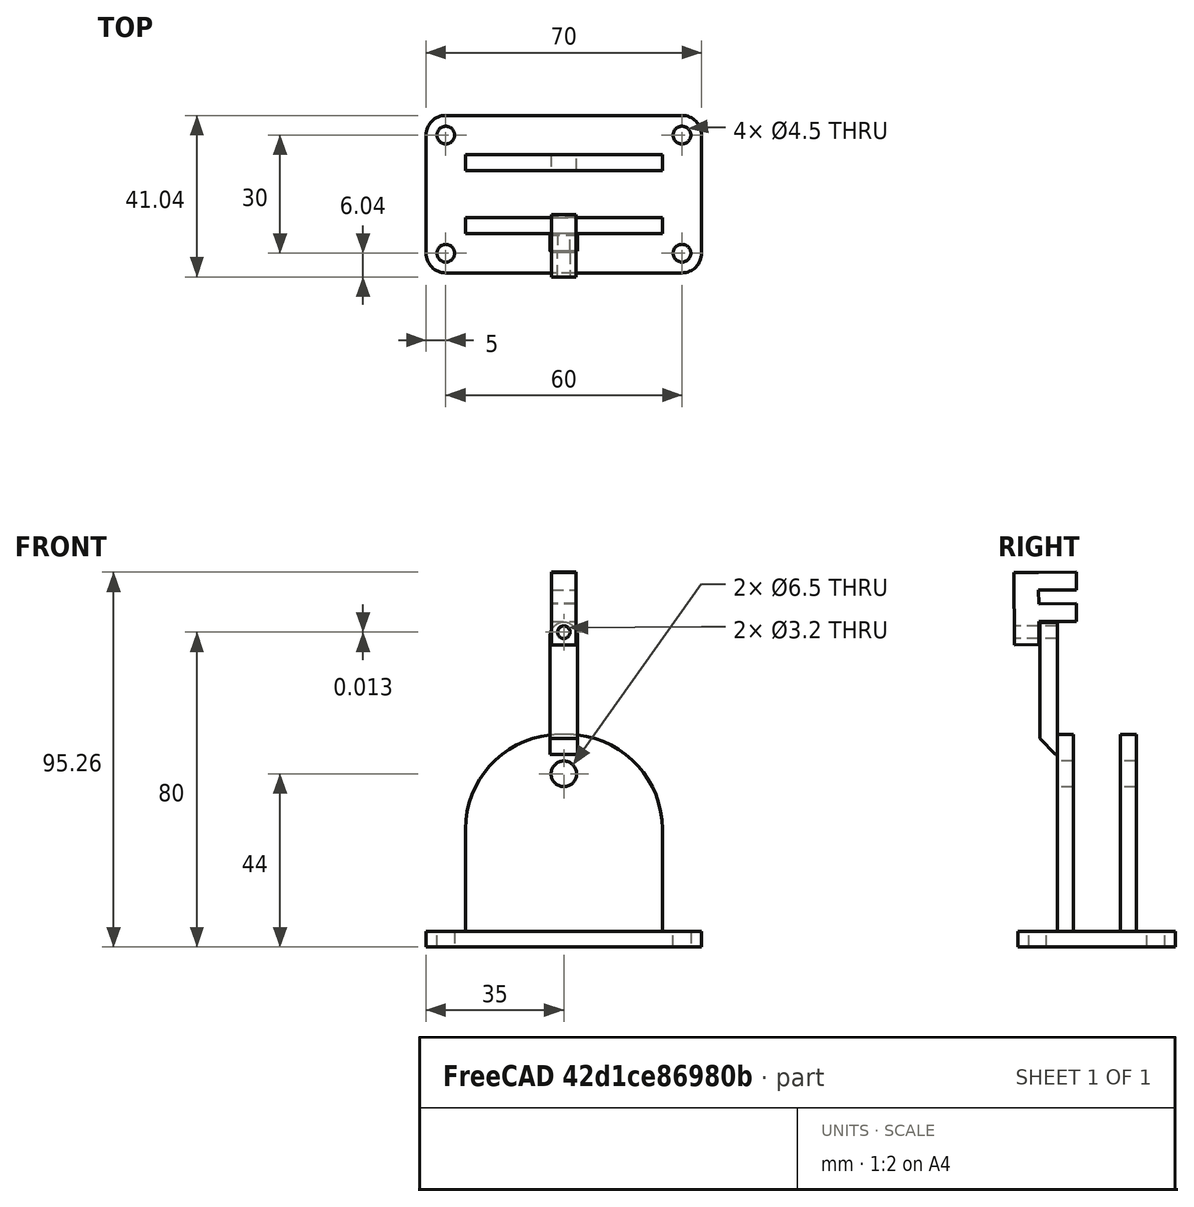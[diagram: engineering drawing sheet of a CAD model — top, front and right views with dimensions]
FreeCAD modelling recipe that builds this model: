
FCSTD DOCUMENT  (FreeCAD 0.18.1R)
Label: Mapa
License: All rights reserved
LicenseURL: http://en.wikipedia.org/wiki/All_rights_reserved
objects: Sketcher::SketchObject×8, PartDesign::Pad×5, PartDesign::Pocket×3, PartDesign::Fillet×2, PartDesign::Body×2, Mesh::Feature×2, PartDesign::Chamfer×1
note: 29 computed .brp shape members not serialized (recipe doc carries the construction recipe); baked Part::Feature solids carry a one-line shape summary decoded from their .brp

FEATURE [Sketcher::SketchObject] Sketch
  MapMode = 5
  Support = -> [XY_Plane]
  sketch-geometry (4):
    g0: LineSegment StartX=-35 StartY=20 StartZ=0 EndX=35 EndY=20 EndZ=0
    g1: LineSegment StartX=35 StartY=20 StartZ=0 EndX=35 EndY=-20 EndZ=0
    g2: LineSegment StartX=35 StartY=-20 StartZ=0 EndX=-35 EndY=-20 EndZ=0
    g3: LineSegment StartX=-35 StartY=-20 StartZ=0 EndX=-35 EndY=20 EndZ=0
  constraints (10):
    c: Coincident(g0,g1)
    c: Coincident(g1,g2)
    c: Coincident(g2,g3)
    c: Coincident(g3,g0)
    c: Horizontal(g2)
    c: Vertical(g3)
    c: Symmetric(g1,g0,g-1)
    c: Symmetric(g0,g0,g-2)
    c: DistanceX(g2,g2) = 70
    c: DistanceY(g1,g1) = 40
FEATURE [PartDesign::Pad] Pad  label="Podstawka"
  Length = 4
  Length2 = 100
  Profile = -> Sketch
  Type = 0
FEATURE [PartDesign::Fillet] Fillet  label="Zaokrąglenie podstawki"
  Base = -> Pad [Edge5,Edge2,Edge8,Edge1]
  BaseFeature = -> Pad
  Radius = 5
FEATURE [Sketcher::SketchObject] Sketch001
  ExternalGeometry = -> [Fillet]
  MapMode = 5
  Placement = pos=(0,0,4) rot=(0,0,1;0rad)
  Support = -> [Fillet]
  sketch-geometry (4):
    g0: Circle CenterX=-30 CenterY=15 CenterZ=0 NormalX=0 NormalY=0 NormalZ=1 AngleXU=0 Radius=2.25
    g1: Circle CenterX=30 CenterY=15 CenterZ=0 NormalX=0 NormalY=0 NormalZ=1 AngleXU=0 Radius=2.25
    g2: Circle CenterX=30 CenterY=-15 CenterZ=0 NormalX=0 NormalY=0 NormalZ=1 AngleXU=0 Radius=2.25
    g3: Circle CenterX=-30 CenterY=-15 CenterZ=0 NormalX=0 NormalY=0 NormalZ=1 AngleXU=0 Radius=2.25
  constraints (9):
    c: Symmetric(g3,g0,g-1)
    c: Symmetric(g0,g1,g-2)
    c: Symmetric(g2,g1,g-1)
    c: Radius(g2) = 2.25
    c: Equal(g2,g1)
    c: Equal(g2,g3)
    c: Equal(g2,g0)
    c: DistanceY(g-3,g2) = 5
    c: DistanceX(g2,g-4) = 5
FEATURE [PartDesign::Pocket] Pocket  label="Dziury montażowe"
  BaseFeature = -> Fillet
  Length = 5
  Length2 = 100
  Offset = 1
  Profile = -> Sketch001
  Type = 2
FEATURE [Sketcher::SketchObject] Sketch002
  ExternalGeometry = -> [Pocket]
  MapMode = 5
  Placement = pos=(0,0,4) rot=(0,0,1;0rad)
  Support = -> [Pocket]
  sketch-geometry (8):
    g0: LineSegment StartX=-25 StartY=10 StartZ=0 EndX=25 EndY=10 EndZ=0
    g1: LineSegment StartX=25 StartY=10 StartZ=0 EndX=25 EndY=6 EndZ=0
    g2: LineSegment StartX=25 StartY=6 StartZ=0 EndX=-25 EndY=6 EndZ=0
    g3: LineSegment StartX=-25 StartY=6 StartZ=0 EndX=-25 EndY=10 EndZ=0
    g4: LineSegment StartX=-25 StartY=-6 StartZ=0 EndX=25 EndY=-6 EndZ=0
    g5: LineSegment StartX=25 StartY=-6 StartZ=0 EndX=25 EndY=-10 EndZ=0
    g6: LineSegment StartX=25 StartY=-10 StartZ=0 EndX=-25 EndY=-10 EndZ=0
    g7: LineSegment StartX=-25 StartY=-10 StartZ=0 EndX=-25 EndY=-6 EndZ=0
  constraints (21):
    c: Coincident(g0,g1)
    c: Coincident(g1,g2)
    c: Coincident(g2,g3)
    c: Coincident(g3,g0)
    c: Horizontal(g0)
    c: Vertical(g1)
    c: Vertical(g3)
    c: Coincident(g4,g5)
    c: Coincident(g5,g6)
    c: Coincident(g6,g7)
    c: Coincident(g7,g4)
    c: Horizontal(g6)
    c: Vertical(g5)
    c: Vertical(g7)
    c: Symmetric(g4,g4,g-2)
    c: Symmetric(g4,g1,g-1)
    c: Symmetric(g2,g1,g-2)
    c: DistanceY(g4,g1) = 12
    c: DistanceY(g5,g5) = 4
    c: Equal(g5,g1)
    c: DistanceX(g0,g0) = 50
FEATURE [PartDesign::Pad] Pad001  label="Scianki"
  BaseFeature = -> Pocket
  Length = 50
  Length2 = 100
  Profile = -> Sketch002
  Type = 0
FEATURE [Sketcher::SketchObject] Sketch003
  ExternalGeometry = -> [Pad001]
  MapMode = 5
  Placement = pos=(0,-10,0) rot=(1,0,0;1.5708rad)
  Support = -> [Pad001]
  sketch-geometry (1):
    g0: Circle CenterX=0 CenterY=44 CenterZ=0 NormalX=0 NormalY=0 NormalZ=1 AngleXU=0 Radius=3.25
  constraints (3):
    c: PointOnObject(g0,g-2)
    c: DistanceY(g-3,g0) = 40
    c: Radius(g0) = 3.25
FEATURE [PartDesign::Pocket] Pocket001  label="Lozysko"
  BaseFeature = -> Pad001
  Length = 5
  Length2 = 100
  Profile = -> Sketch003
  Type = 1
FEATURE [PartDesign::Fillet] Fillet001  label="Zaokrąglenie"
  Base = -> Pocket001 [Edge54,Edge64,Edge50,Edge60]
  BaseFeature = -> Pocket001
  Radius = 24
FEATURE [Sketcher::SketchObject] Sketch004
  MapMode = 5
  Support = -> [XY_Plane001]
  sketch-geometry (6):
    g0: LineSegment StartX=-3.1 StartY=9.2 StartZ=0 EndX=3.1 EndY=9.2 EndZ=0
    g1: LineSegment StartX=3.1 StartY=9.2 StartZ=0 EndX=3.1 EndY=-9.2 EndZ=0
    g2: LineSegment StartX=3.1 StartY=-9.2 StartZ=0 EndX=-3.1 EndY=-9.2 EndZ=0
    g3: LineSegment StartX=-3.1 StartY=-9.2 StartZ=0 EndX=-3.1 EndY=9.2 EndZ=0
    g4: Circle CenterX=0 CenterY=-6 CenterZ=0 NormalX=0 NormalY=0 NormalZ=1 AngleXU=0 Radius=1.6
    g5: GeomPoint X=0 Y=-7.6 Z=0
  constraints (15):
    c: Coincident(g0,g1)
    c: Coincident(g1,g2)
    c: Coincident(g2,g3)
    c: Coincident(g3,g0)
    c: Horizontal(g2)
    c: Vertical(g3)
    c: DistanceX(g2,g2) = 6.2
    c: DistanceY(g1,g1) = 18.4
    c: Symmetric(g0,g0,g-2)
    c: Symmetric(g1,g0,g-1)
    c: PointOnObject(g4,g-2)
    c: Radius(g4) = 1.6
    c: PointOnObject(g5,g4)
    c: PointOnObject(g5,g-2)
    c: DistanceY(g1,g5) = 1.6
FEATURE [PartDesign::Pad] Pad002
  Length = 6.25
  Length2 = 100
  Profile = -> Sketch004
  Type = 0
FEATURE [Sketcher::SketchObject] Sketch005
  ExternalGeometry = -> [Pad002]
  MapMode = 5
  Placement = pos=(0,0,6.25) rot=(0,0,1;0rad)
  Support = -> [Pad002]
  sketch-geometry (8):
    g0: LineSegment StartX=-3.1 StartY=9.2 StartZ=0 EndX=3.1 EndY=9.2 EndZ=0
    g1: LineSegment StartX=3.1 StartY=9.2 StartZ=0 EndX=3.1 EndY=4.7 EndZ=0
    g2: LineSegment StartX=3.1 StartY=4.7 StartZ=0 EndX=-3.1 EndY=4.7 EndZ=0
    g3: LineSegment StartX=-3.1 StartY=4.7 StartZ=0 EndX=-3.1 EndY=9.2 EndZ=0
    g4: LineSegment StartX=-3.1 StartY=1.2 StartZ=0 EndX=3.1 EndY=1.2 EndZ=0
    g5: LineSegment StartX=3.1 StartY=1.2 StartZ=0 EndX=3.1 EndY=-3.3 EndZ=0
    g6: LineSegment StartX=3.1 StartY=-3.3 StartZ=0 EndX=-3.1 EndY=-3.3 EndZ=0
    g7: LineSegment StartX=-3.1 StartY=-3.3 StartZ=0 EndX=-3.1 EndY=1.2 EndZ=0
  constraints (23):
    c: Coincident(g0,g1)
    c: Coincident(g1,g2)
    c: Coincident(g2,g3)
    c: Coincident(g3,g0)
    c: Horizontal(g0)
    c: Horizontal(g2)
    c: Vertical(g1)
    c: Vertical(g3)
    c: Coincident(g0,g-4)
    c: PointOnObject(g1,g-5)
    c: Coincident(g4,g5)
    c: Coincident(g5,g6)
    c: Coincident(g6,g7)
    c: Coincident(g7,g4)
    c: Horizontal(g4)
    c: Horizontal(g6)
    c: Vertical(g5)
    c: Vertical(g7)
    c: PointOnObject(g4,g-4)
    c: PointOnObject(g5,g-5)
    c: DistanceY(g3,g3) = 4.5
    c: Equal(g7,g3)
    c: DistanceY(g4,g2) = 3.5
FEATURE [PartDesign::Pad] Pad003
  BaseFeature = -> Pad002
  Length = 9.6
  Length2 = 100
  Profile = -> Sketch005
  Type = 0
FEATURE [PartDesign::Body] Body001  label="Czujnik"
  Group = -> [Sketch004,Pad002,Sketch005,Pad003]
  Origin = -> Origin001
  Placement = pos=(0,-21,86) rot=(0,0.705662,0.708549;3.14159rad)
  Tip = -> Pad003
FEATURE [Mesh::Feature] kolo3
  Placement = pos=(0,0,44) rot=(1,0,0;1.5708rad)
FEATURE [Mesh::Feature] kolo_duze  label="kolo-duze"
  Placement = pos=(-0.54,-1.5,439.15) rot=(-0.992807,0.084658,0.084658;1.57801rad)
FEATURE [Sketcher::SketchObject] Sketch006
  ExternalGeometry = -> [Fillet001]
  MapMode = 5
  Placement = pos=(0,-10,0) rot=(1,0,0;1.5708rad)
  Support = -> [Fillet001]
  sketch-geometry (5):
    g0: LineSegment StartX=3.5 StartY=49 StartZ=0 EndX=-3.5 EndY=49 EndZ=0
    g1: ArcOfCircle CenterX=0 CenterY=79 CenterZ=0 NormalX=0 NormalY=0 NormalZ=1 AngleXU=0 Radius=3.5 StartAngle=-1.8e-15 EndAngle=3.14159
    g2: GeomPoint X=0 Y=82.5 Z=0
    g3: LineSegment StartX=-3.5 StartY=79 StartZ=0 EndX=-3.5 EndY=49 EndZ=0
    g4: LineSegment StartX=3.5 StartY=49 StartZ=0 EndX=3.5 EndY=79 EndZ=0
  constraints (14):
    c: Symmetric(g0,g0,g-2)
    c: DistanceX(g0,g0) = 7
    c: DistanceY(g0,g-3) = 5
    c: PointOnObject(g1,g-2)
    c: Horizontal(g1,g1)
    c: Horizontal(g1,g1)
    c: PointOnObject(g2,g1)
    c: DistanceY(g0,g2) = 33.5
    c: Coincident(g3,g1)
    c: Coincident(g3,g0)
    c: Vertical(g3)
    c: Coincident(g4,g0)
    c: Coincident(g4,g1)
    c: PointOnObject(g2,g-2)
FEATURE [PartDesign::Pad] Pad004  label="Rączka"
  BaseFeature = -> Fillet001
  Length = 4.5
  Length2 = 100
  Profile = -> Sketch006
  Type = 0
FEATURE [PartDesign::Chamfer] Chamfer  label="Redukcja nadwisu"
  Base = -> Pad004 [Edge89]
  BaseFeature = -> Pad004
  Size = 4
FEATURE [Sketcher::SketchObject] Sketch007
  ExternalGeometry = -> [Chamfer]
  MapMode = 5
  Placement = pos=(0,-14.5,3.4e-15) rot=(1,0,0;1.5708rad)
  Support = -> [Chamfer]
  sketch-geometry (2):
    g0: Circle CenterX=0 CenterY=80 CenterZ=0 NormalX=0 NormalY=0 NormalZ=1 AngleXU=0 Radius=1.6
    g1: GeomPoint X=0 Y=81.6 Z=0
  constraints (5):
    c: PointOnObject(g0,g-2)
    c: Radius(g0) = 1.6
    c: PointOnObject(g1,g0)
    c: PointOnObject(g1,g-2)
    c: DistanceY(g-5,g0) = 1
FEATURE [PartDesign::Pocket] Pocket002  label="Otwór na czujnik"
  BaseFeature = -> Chamfer
  Length = 5
  Length2 = 100
  Profile = -> Sketch007
  Type = 2
FEATURE [PartDesign::Body] Body  label="Uchwyt"
  Group = -> [Sketch,Pad,Fillet,Sketch001,Pocket,Sketch002,Pad001,Sketch003,Pocket001,Fillet001,Sketch006,Pad004,Chamfer,Sketch007,Pocket002]
  Origin = -> Origin
  Tip = -> Pocket002
